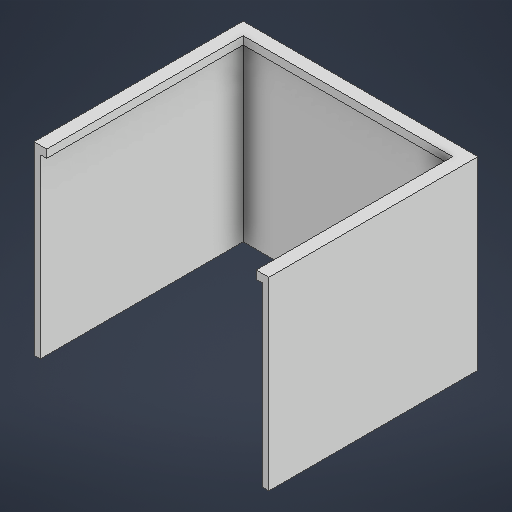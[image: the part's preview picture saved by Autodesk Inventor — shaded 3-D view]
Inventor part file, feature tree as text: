
AUTODESK INVENTOR PART (.ipt)
format: ipt  version: 2025 (Build 290162000, 162)  size: 187,392 bytes
history: native  units: in
note: dims shown in document units (in); Inventor stores cm internally (conversion verified against a paired STEP export)
features: extrude x3, sketch x3
ambient origin geometry x8: Origin, YZ Plane, XZ Plane, XY Plane, X Axis, Y Axis, Z Axis, Center Point
bodies: Solid1 (feature_tree)
feature tree (6):
  extrude  "Extrusion1"  Depth=5.1181in
  extrude  "Extrusion2"  Depth=5.4429in
  extrude  "Extrusion3"  Depth=5.4429in
  sketch  "Sketch1"  dims[d0=5.748in d1=5.1181in]
  sketch  "Sketch2"  dims[d2=4.5276in d3=0.0in d4=5.4429in]
  sketch  "Sketch3"  dims[d5=4.813in d6=5.4429in d7=1.1811in d8=0.0in d9=0.0in d10=0.1575in d11=0.1575in d12=0.1969in d13=0.0in]
